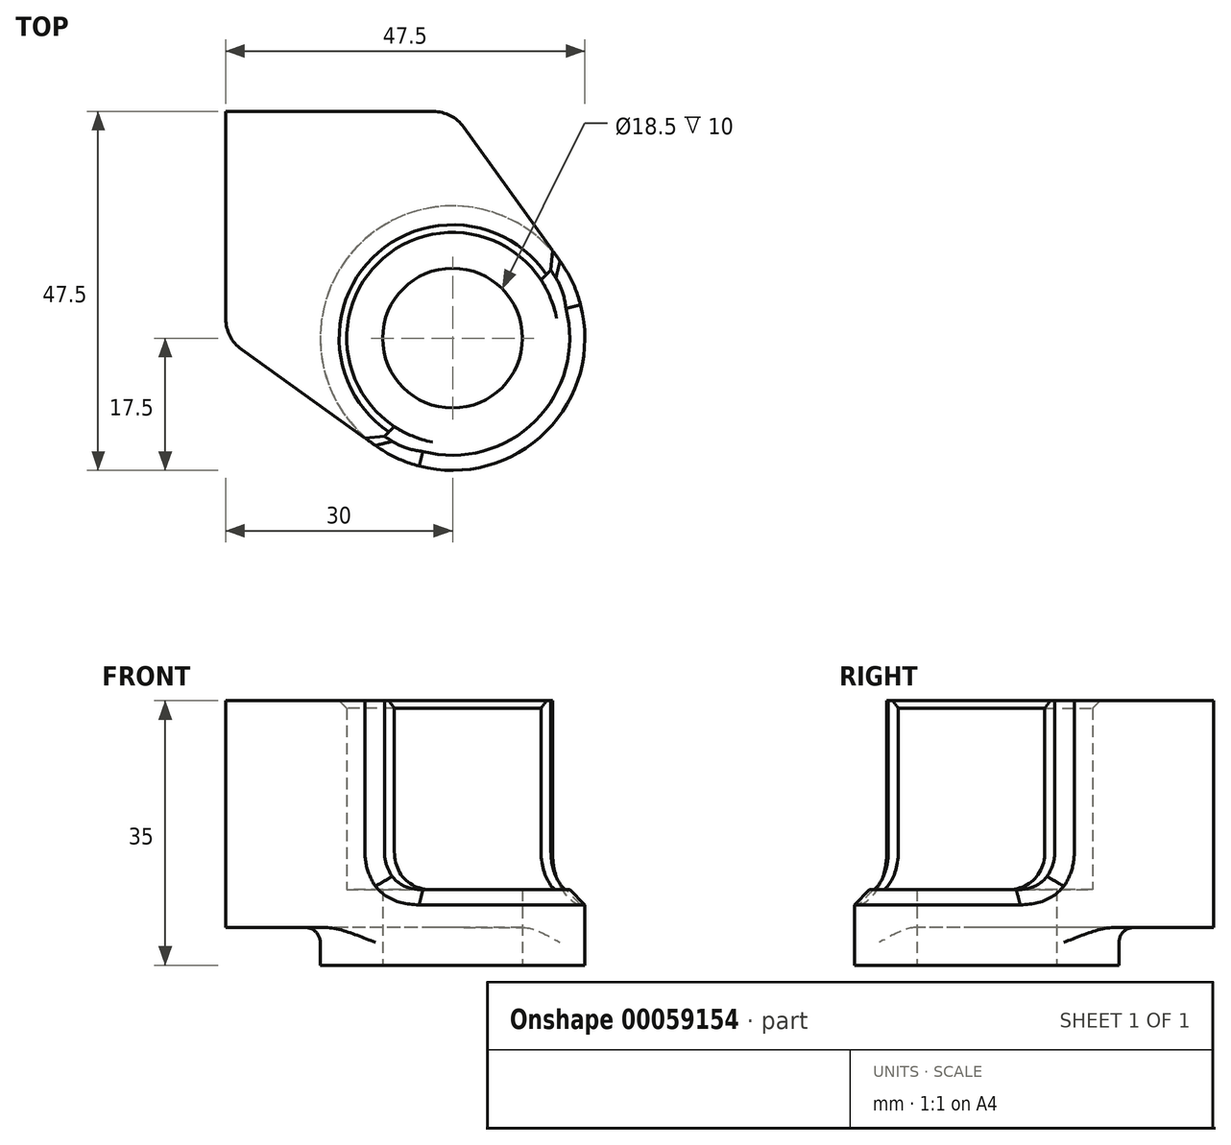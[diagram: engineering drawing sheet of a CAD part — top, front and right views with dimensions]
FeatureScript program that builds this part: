
annotation { "Feature Type Name" : "Feature", "Feature Type Description" : "" }
export const myFeature = defineFeature(function(context is Context, id is Id, definition is map)
    precondition{}
    {
        {
            var Q0;
            Q0=qCreatedBy(makeId("Top.planeOp"),FACE);
            var sketch = newSketch(context, id + "F0", { "sketchPlane" : qUnion([Q0])});
            skCircle(sketch, "E0", {"center": v(0, 0) * mm, "radius": 9.25 * mm});
            skCircle(sketch, "E1", {"center": v(0, 0) * mm, "radius": 17.5 * mm});
            skSolve(sketch);
        }
        {
            var Q0;
            Q0=makeQuery(id+"F0.imprint","IMPRINT",FACE,{"disambiguationData":[TD([[makeQuery(id+"F0.imprint","IMPRINT",EDGE,{"derivedFrom":sQuery(id+"F0.wireOp",EDGE,"E0")}),-1.0]])]});
            extrude(context, id + "F1", {"entities" : qUnion([Q0]), "depth" : 10 * mm});
        }
        {
            var Q0;
            Q0=makeQuery(id+"F1.opExtrude","CAP_FACE",FACE,{"disambiguationData":[OSD([sQuery(id+"F0.wireOp",EDGE,"E0"),sQuery(id+"F0.wireOp",EDGE,"E1")])],"isStart":false});
            var sketch = newSketch(context, id + "F2", { "sketchPlane" : qUnion([Q0])});
            skLineSegment(sketch, "E2.top", {"start": v(0, 30) * mm, "end": v(-30, 30) * mm});
            skLineSegment(sketch, "E3", {"start": v(-30, 30) * mm, "end": v(-30, 0) * mm});
            skLineSegment(sketch, "E4", {"start": v(-30, 0) * mm, "end": v(-10.2, -14.21) * mm});
            skLineSegment(sketch, "E5", {"start": v(0, 30) * mm, "end": v(14.21, 10.2) * mm});
            skArc(sketch, "E6", {"start": v(11.7, 7.7) * mm, "mid": v(-9.9, 9.9) * mm, "end": v(-7.7, -11.7) * mm});
            skLineSegment(sketch, "E7", {"start": v(14.21, 10.2) * mm, "end": v(11.7, 7.7) * mm});
            skLineSegment(sketch, "E8.trimOffspring", {"start": v(-7.7, -11.7) * mm, "end": v(-10.2, -14.21) * mm});
            skSolve(sketch);
        }
        {
            var Q0;
            Q0=makeQuery(id+"F2.imprint","IMPRINT",FACE,{"disambiguationData":[TD([[makeQuery(id+"F2.imprint","IMPRINT",EDGE,{"derivedFrom":sQuery(id+"F2.wireOp",EDGE,"E2.top")}),1.0]])]});
            var Q1;
            Q1=makeQuery(id+"F2.imprint","IMPRINT",FACE,{"disambiguationData":[TD([[makeQuery(id+"F2.imprint","IMPRINT",EDGE,{"derivedFrom":sQuery(id+"F2.wireOp",EDGE,"E6")}),-1.0]])]});
            extrude(context, id + "F3", {"entities" : qUnion([Q0, Q1]), "operationType" : NewBodyOperationType.ADD, "depth" : 25 * mm, "hasSecondDirection" : true, "secondDirectionOppositeDirection" : true, "secondDirectionDepth" : 5 * mm});
        }
        {
            var Q0;
            Q0=makeQuery(id+"F3.boolean.opBoolean","INTERSECT",EDGE,{"derivedFrom":[makeQuery(id+"F1.opExtrude","SWEPT_FACE",FACE,{"disambiguationData":[OSD([sQuery(id+"F0.wireOp",EDGE,"E1")])]}),makeQuery(id+"F3.opExtrude","CAP_FACE",FACE,{"disambiguationData":[OSD([sQuery(id+"F2.wireOp",EDGE,"E2.top"),sQuery(id+"F2.wireOp",EDGE,"E3"),sQuery(id+"F2.wireOp",EDGE,"E4"),sQuery(id+"F2.wireOp",EDGE,"E5"),sQuery(id+"F2.wireOp",EDGE,"E6"),sQuery(id+"F2.wireOp",EDGE,"E7"),sQuery(id+"F2.wireOp",EDGE,"E8.trimOffspring")])],"isStart":true})]});
            fillet(context, id + "F4", {"entities" : qUnion([Q0]), "radius" : 2 * mm, "tangentPropagation" : true, "allowEdgeOverflow" : false});
        }
        {
            var Q0;
            Q0=makeQuery(id+"F3.opExtrude","SWEPT_EDGE",EDGE,{"disambiguationData":[OSD([sQuery(id+"F2.wireOp",EDGE,"E3"),sQuery(id+"F2.wireOp",EDGE,"E4")])]});
            var Q1;
            Q1=makeQuery(id+"F3.opExtrude","SWEPT_EDGE",EDGE,{"disambiguationData":[OSD([sQuery(id+"F2.wireOp",EDGE,"E2.top"),sQuery(id+"F2.wireOp",EDGE,"E5")])]});
            fillet(context, id + "F5", {"entities" : qUnion([Q0, Q1]), "radius" : 5 * mm, "tangentPropagation" : true, "allowEdgeOverflow" : false});
        }
        {
            var Q0;
            Q0=makeQuery(id+"F3.boolean.opBoolean","INTERSECT",EDGE,{"derivedFrom":[makeQuery(id+"F1.opExtrude","CAP_FACE",FACE,{"disambiguationData":[OSD([sQuery(id+"F0.wireOp",EDGE,"E0"),sQuery(id+"F0.wireOp",EDGE,"E1")])],"isStart":false}),makeQuery(id+"F3.opExtrude","SWEPT_FACE",FACE,{"disambiguationData":[OSD([sQuery(id+"F2.wireOp",EDGE,"E8.trimOffspring")])]})]});
            var Q1;
            Q1=makeQuery(id+"F3.boolean.opBoolean","INTERSECT",EDGE,{"derivedFrom":[makeQuery(id+"F1.opExtrude","CAP_FACE",FACE,{"disambiguationData":[OSD([sQuery(id+"F0.wireOp",EDGE,"E0"),sQuery(id+"F0.wireOp",EDGE,"E1")])],"isStart":false}),makeQuery(id+"F3.opExtrude","SWEPT_FACE",FACE,{"disambiguationData":[OSD([sQuery(id+"F2.wireOp",EDGE,"E7")])]})]});
            fillet(context, id + "F6", {"entities" : qUnion([Q0, Q1]), "radius" : 5 * mm, "tangentPropagation" : true, "allowEdgeOverflow" : false});
        }
        {
            var Q0;
            Q0=makeQuery(id+"F1.opExtrude","CAP_EDGE",EDGE,{"disambiguationData":[OSD([sQuery(id+"F0.wireOp",EDGE,"E1")])],"isStart":false});
            chamfer(context, id + "F7", {"entities" : qUnion([Q0]), "width" : 2 * mm, "tangentPropagation" : true});
        }
        {
            var Q0;
            Q0=makeQuery(id+"F3.opExtrude","CAP_EDGE",EDGE,{"disambiguationData":[OSD([sQuery(id+"F2.wireOp",EDGE,"E6")])],"isStart":false});
            chamfer(context, id + "F8", {"entities" : qUnion([Q0]), "width" : 1 * mm, "tangentPropagation" : true});
        }
    });
